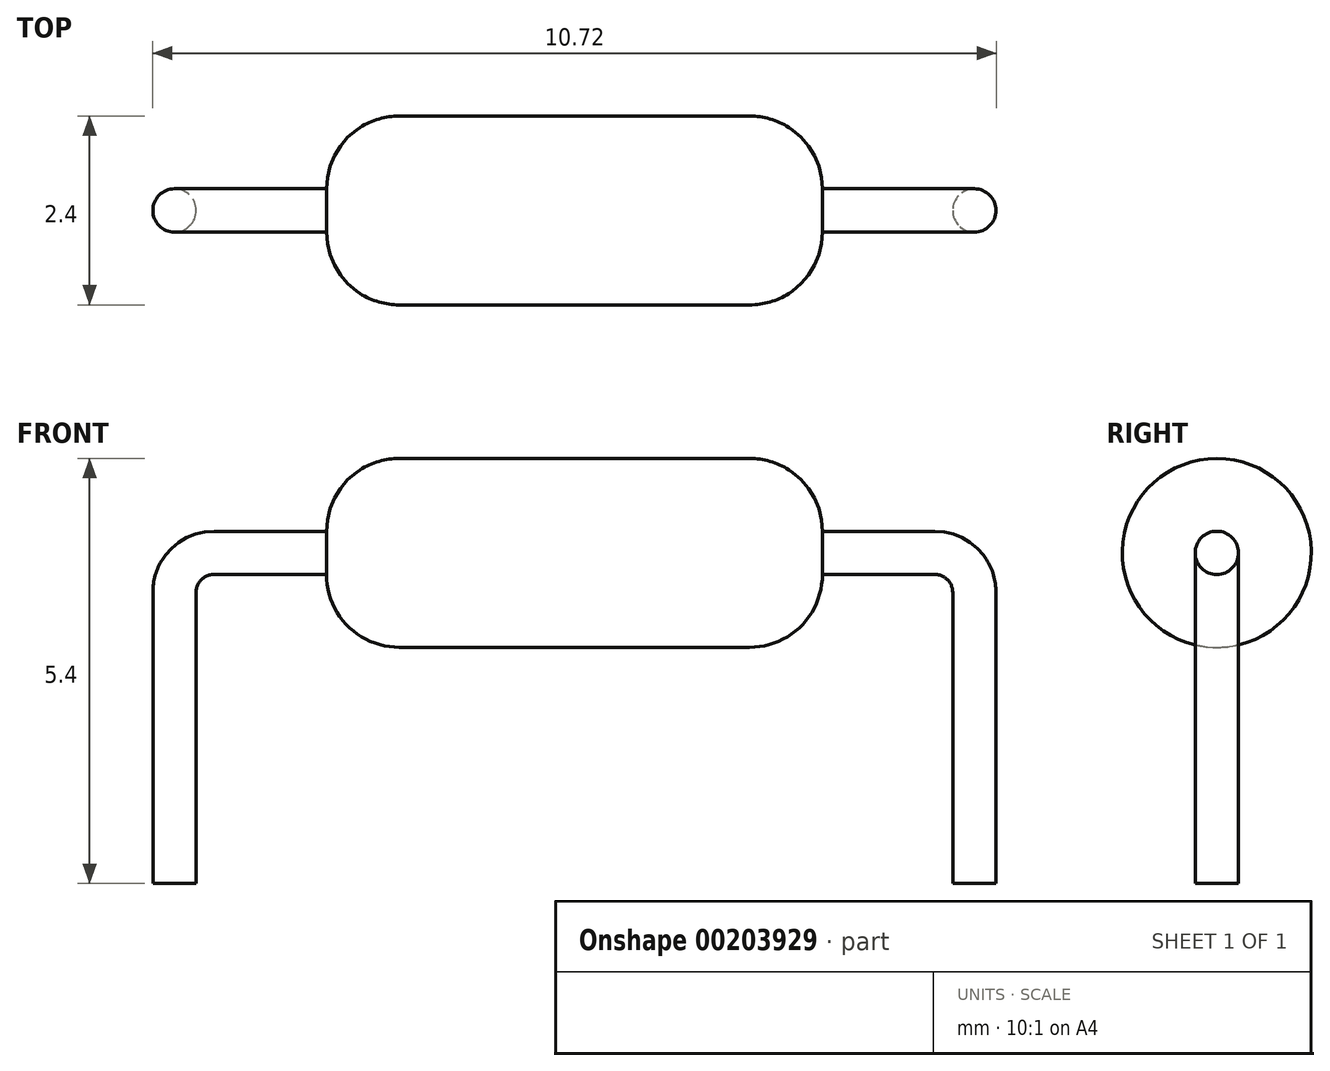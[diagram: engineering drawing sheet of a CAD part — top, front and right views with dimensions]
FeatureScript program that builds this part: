
annotation { "Feature Type Name" : "Feature", "Feature Type Description" : "" }
export const myFeature = defineFeature(function(context is Context, id is Id, definition is map)
    precondition{}
    {
        {
            var Q0;
            Q0=qCreatedBy(makeId("Right.planeOp"),FACE);
            var sketch = newSketch(context, id + "F0", { "sketchPlane" : qUnion([Q0])});
            skCircle(sketch, "E0", {"center": v(0, 0) * mm, "radius": 1.2 * mm});
            skSolve(sketch);
        }
        {
            var Q0;
            Q0=makeQuery(id+"F0.imprint","IMPRINT",FACE,{"disambiguationData":[TD([[makeQuery(id+"F0.imprint","IMPRINT",EDGE,{"derivedFrom":sQuery(id+"F0.wireOp",EDGE,"E0")}),1.0]])]});
            extrude(context, id + "F1", {"entities" : qUnion([Q0]), "offsetDistance" : 25 * mm, "depth" : 3.15 * mm});
        }
        {
            var Q0;
            Q0=makeQuery(id+"F1.opExtrude","CAP_EDGE",EDGE,{"disambiguationData":[OSD([sQuery(id+"F0.wireOp",EDGE,"E0")])],"isStart":false});
            fillet(context, id + "F2", {"entities" : qUnion([Q0]), "radius" : 0.93 * mm, "tangentPropagation" : true, "allowEdgeOverflow" : false});
        }
        {
            var Q0;
            Q0=makeQuery(id+"F1.opExtrude","CAP_FACE",FACE,{"disambiguationData":[OSD([sQuery(id+"F0.wireOp",EDGE,"E0")])],"isStart":false});
            var sketch = newSketch(context, id + "F3", { "sketchPlane" : qUnion([Q0])});
            skCircle(sketch, "E1", {"center": v(0, 0) * mm, "radius": 0.28 * mm});
            skSolve(sketch);
        }
        {
            var Q0;
            Q0=qCreatedBy(makeId("Front.planeOp"),FACE);
            var sketch = newSketch(context, id + "F4", { "sketchPlane" : qUnion([Q0])});
            skLineSegment(sketch, "E2", {"start": v(4.58, 0) * mm, "end": v(3.15, 0) * mm});
            skLineSegment(sketch, "E3", {"start": v(5.08, -0.5) * mm, "end": v(5.08, -4.2) * mm});
            skPoint(sketch, "E4.visualSharp", {"position": v(5.08, 0) * mm});
            skArc(sketch, "E4.filletArc", {"start": v(5.08, -0.5) * mm, "mid": v(4.93, -0.15) * mm, "end": v(4.58, 0) * mm});
            skSolve(sketch);
        }
        {
            var Q0;
            Q0=makeQuery(id+"F3.imprint","IMPRINT",FACE,{"disambiguationData":[TD([[makeQuery(id+"F3.imprint","IMPRINT",EDGE,{"derivedFrom":sQuery(id+"F3.wireOp",EDGE,"E1")}),1.0]])]});
            var Q1;
            Q1=sQuery(id+"F4.wireOp",EDGE,"E2");
            var Q2;
            Q2=sQuery(id+"F4.wireOp",EDGE,"E4.filletArc");
            var Q3;
            Q3=sQuery(id+"F4.wireOp",EDGE,"E3");
            sweep(context, id + "F5", {"operationType" : NewBodyOperationType.ADD, "profiles" : qUnion([Q0]), "path" : qUnion([Q1, Q2, Q3])});
        }
        {
            var Q0;
            Q0=makeQuery(id+"F1.opExtrude","SWEPT_BODY",BODY,{"disambiguationData":[OSD([sQuery(id+"F0.wireOp",EDGE,"E0")])]});
            var Q1;
            Q1=makeQuery(id+"F1.opExtrude","CAP_FACE",FACE,{"disambiguationData":[OSD([sQuery(id+"F0.wireOp",EDGE,"E0")])],"isStart":true});
            mirror(context, id + "F6", {"operationType" : NewBodyOperationType.ADD, "entities" : qUnion([Q0]), "mirrorPlane" : qUnion([Q1])});
        }
    });
